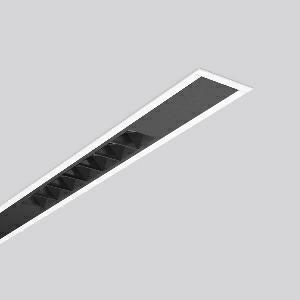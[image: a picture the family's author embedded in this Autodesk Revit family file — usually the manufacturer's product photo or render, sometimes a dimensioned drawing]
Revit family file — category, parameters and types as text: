
# Revit family: less_is_more_beamline_312474_002_c138
name_source: partatom
category: Lighting Fixtures
units: mm (PartAtom-declared; Revit-internal decimal feet)

## family parameters
Cut with Voids When Loaded = No
Host = Face
Light Source = No
Part Type = Normal
Room Calculation Point = No
Round Connector Dimension = Use Diameter
Shared = No

## types (1)
- LESS IS MORE BEAMLINE (1 x LED Modul 930, 1783.33 lm, 3000)
    Apparent Load = 72 VA
    CIE Flux Codes = 100 100 100 100 100
    Color Rendering = 90
    Color Temperature = 3000
    Default Elevation = 1800 mm
    Description = Series: LESS IS MORE BEAMLINE
Linear recessed ceiling and wall luminaire for aesthetically sophisticated lighting. Luminaire with three LED light units. Housing: extruded aluminium profile, powder-coated. End cap aluminium powder-coated. LED light unit with MRS technology: Mini-Reflector-System made of metallised thermoplastic with prismatic black glare-suppressing frame for pleasant glare-free light (RUG < 10). Each LED light unit has 7 reflector elements. Narrow beam light distribution. Ceiling installation with pre-assembled SBS mounting system. LED unit with integrated converter interchangeable and removable. Suitable for through-wiring. 
Colour: traffic white, matt (RAL 9016)
Length: 1702 mm
Width: 71 mm
Height: 1.5 mm
Cut-out length: 1688 mm
Cut-out width: 60 mm
Recess height: 125 mm
Luminaire: recess height: 106 mm
Lamp: LED
Socket: without socket
Colour temperature: 3000K
Colour rendering index (CRI): 90
System power: 72 W
Rated luminous flux: 5350 lm
Luminous efficiency: 74 lm/W
Control gear: Regulated power supply
Protection class: I
Type of protection: IP 20
    Height = 0 mm  [stored 0 ft]
    Lamp = 1 x LED Modul 930
    Lamp Light Flux = 1783.33 lm
    Lamp count = 1
    Length = 1702 mm
    Lifetime = 50000 h
    Luminous efficacy = 74 lm/W
    Manufacturer = RZB
    ModVariant = No
    Model = 312474.002
    Mounting Place = Ceiling, Wall
    Mounting Type = Recessed
    Number of Poles = 1
    OnlyDefault = Yes
    Power Factor = 1
    Product Name = LESS IS MORE BEAMLINE
    Product group = Recessed LED linear luminaires
    ProductGroupID = 407
    Protection Class = Protection class I
    Protection Degree = IP 20
    RLX_Detail_Level = 1
    RLX_Emergency_Light_Flux = 0 lm
    RLX_Emergency_Type = 0
    RLX_Emergency_Type_DB = No
    RlxData = <blob elided: 24041 chars, md5=57da8d81>
    Socket = socket
    Standby Power = 0 W
    System Light Flux = 5350 lm
    System Power = 72 W
    Type Comments = Product without accessories
    Type Image = 312465.002.jpg
    URL = http://relux.com
    VarID = ---
    Voltage = 230 V
    Voltage Range = 220-240 V
    Weight = 0.00 kg
    Width = 71 mm

note: [stored X ft] marks values corroborated as IEEE doubles in the binary element streams (Revit-internal decimal feet)

## geometry (parser evidence)
native form markers: Blend x4, Sweep x17
no freeform markers — native parametric forms only
